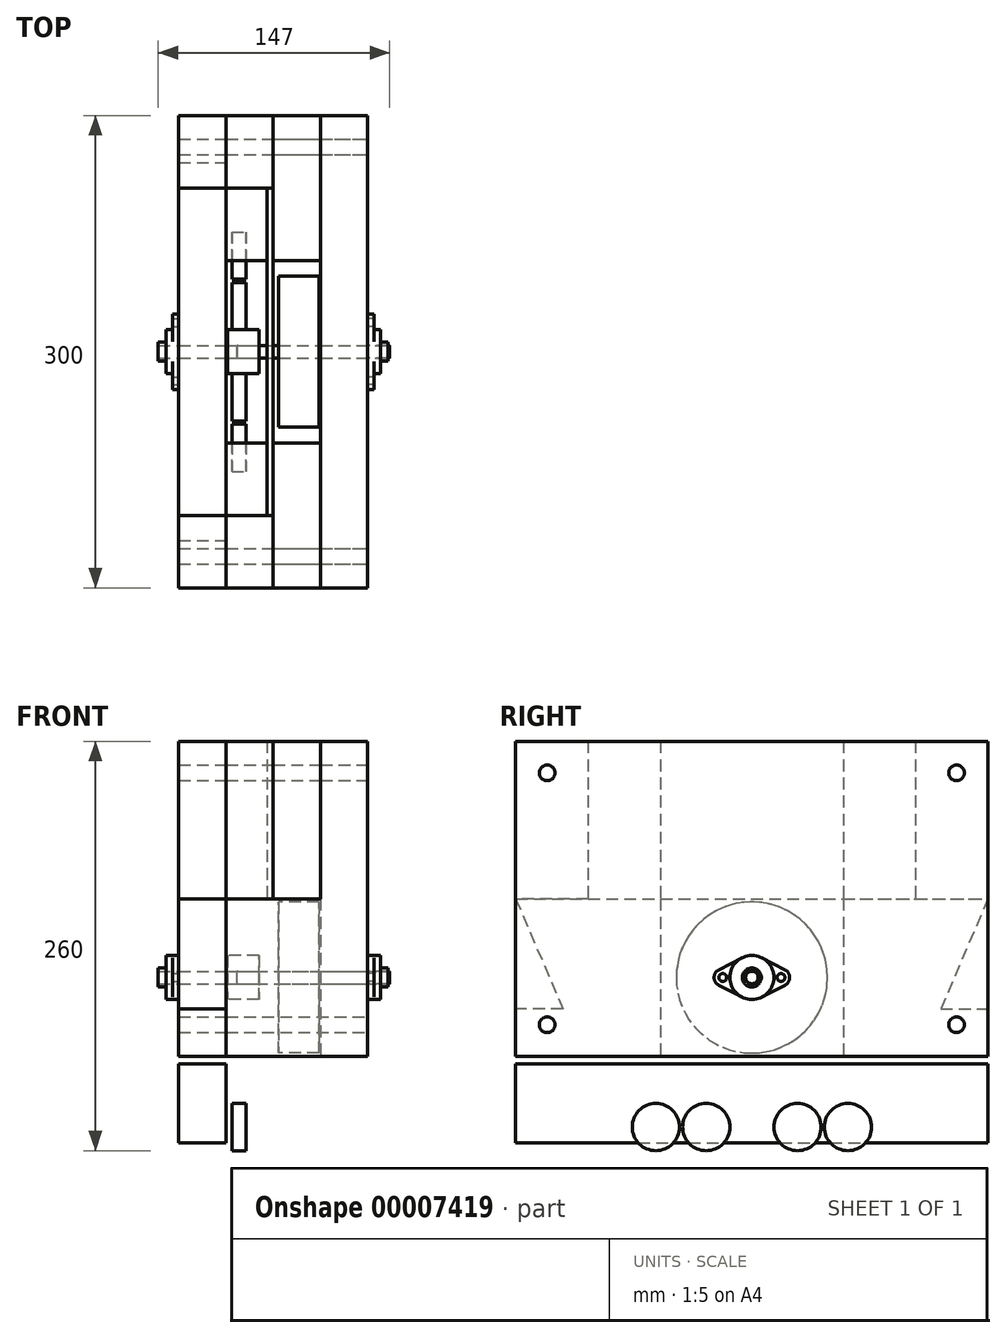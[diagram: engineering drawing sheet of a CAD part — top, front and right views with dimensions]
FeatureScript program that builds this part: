
annotation { "Feature Type Name" : "Feature", "Feature Type Description" : "" }
export const myFeature = defineFeature(function(context is Context, id is Id, definition is map)
    precondition{}
    {
        {
            var Q0;
            Q0=qCreatedBy(makeId("Front.planeOp"),FACE);
            var sketch = newSketch(context, id + "F0", { "sketchPlane" : qUnion([Q0])});
            skLineSegment(sketch, "E0.bottom", {"start": v(10, 14) * mm, "end": v(-10, 14) * mm});
            skLineSegment(sketch, "E0.top", {"start": v(10, -14) * mm, "end": v(4.5, -14) * mm});
            skLineSegment(sketch, "E0.left", {"start": v(10, 14) * mm, "end": v(10, -14) * mm});
            skLineSegment(sketch, "E0.right", {"start": v(-10, 14) * mm, "end": v(-10, -14) * mm});
            skPoint(sketch, "E0.middle", {"position": v(0, 0) * mm});
            skLineSegment(sketch, "E1", {"start": v(0, 0) * mm, "end": v(134.05, 0) * mm, "construction": true});
            skLineSegment(sketch, "E2", {"start": v(0, 0) * mm, "end": v(-79.2, 0) * mm, "construction": true});
            skLineSegment(sketch, "E3.bottom", {"start": v(-41, 15) * mm, "end": v(-56, 15) * mm});
            skLineSegment(sketch, "E3.top", {"start": v(-41, -15) * mm, "end": v(-56, -15) * mm});
            skLineSegment(sketch, "E3.left", {"start": v(-41, 15) * mm, "end": v(-41, -15) * mm});
            skLineSegment(sketch, "E3.right", {"start": v(-56, 15) * mm, "end": v(-56, -15) * mm});
            skPoint(sketch, "E3.middle", {"position": v(-48.5, 0) * mm});
            skLineSegment(sketch, "E4.bottom", {"start": v(48, 48) * mm, "end": v(32.5, 48) * mm});
            skLineSegment(sketch, "E4.top", {"start": v(48, -48) * mm, "end": v(22.5, -48) * mm});
            skLineSegment(sketch, "E4.left", {"start": v(48, 48) * mm, "end": v(48, -48) * mm});
            skLineSegment(sketch, "E4.right", {"start": v(22.5, 48) * mm, "end": v(22.5, -48) * mm});
            skPoint(sketch, "E4.middle", {"position": v(35.25, 0) * mm});
            skLineSegment(sketch, "E5.bottom", {"start": v(94, 15) * mm, "end": v(79, 15) * mm});
            skLineSegment(sketch, "E5.top", {"start": v(94, -15) * mm, "end": v(79, -15) * mm});
            skLineSegment(sketch, "E5.left", {"start": v(94, 15) * mm, "end": v(94, -15) * mm});
            skLineSegment(sketch, "E5.right", {"start": v(79, 15) * mm, "end": v(79, -15) * mm});
            skPoint(sketch, "E5.middle", {"position": v(86.5, 0) * mm});
            skLineSegment(sketch, "E6.bottom", {"start": v(24, 127.89) * mm, "end": v(54, 127.89) * mm});
            skLineSegment(sketch, "E6.top", {"start": v(24, 77.89) * mm, "end": v(54, 77.89) * mm});
            skLineSegment(sketch, "E6.left", {"start": v(24, 127.89) * mm, "end": v(24, 77.89) * mm});
            skLineSegment(sketch, "E6.right", {"start": v(54, 127.89) * mm, "end": v(54, 77.89) * mm});
            skLineSegment(sketch, "E7", {"start": v(54, 77.89) * mm, "end": v(64, 77.89) * mm});
            skLineSegment(sketch, "E8", {"start": v(64, 77.89) * mm, "end": v(64, 127.89) * mm});
            skLineSegment(sketch, "E9", {"start": v(64, 127.89) * mm, "end": v(54, 127.89) * mm});
            skLineSegment(sketch, "E10.bottom", {"start": v(79, 50) * mm, "end": v(49, 50) * mm});
            skLineSegment(sketch, "E10.top", {"start": v(79, -50) * mm, "end": v(49, -50) * mm});
            skLineSegment(sketch, "E10.left", {"start": v(79, 50) * mm, "end": v(79, -50) * mm});
            skLineSegment(sketch, "E10.right", {"start": v(49, 50) * mm, "end": v(49, -50) * mm});
            skPoint(sketch, "E10.middle", {"position": v(64, 0) * mm});
            skLineSegment(sketch, "E11.bottom", {"start": v(-11, 50) * mm, "end": v(-41, 50) * mm});
            skLineSegment(sketch, "E11.top", {"start": v(-11, -50) * mm, "end": v(-41, -50) * mm});
            skLineSegment(sketch, "E11.left", {"start": v(-11, 50) * mm, "end": v(-11, -50) * mm});
            skLineSegment(sketch, "E11.right", {"start": v(-41, 50) * mm, "end": v(-41, -50) * mm});
            skPoint(sketch, "E11.middle", {"position": v(-26, 0) * mm});
            skLineSegment(sketch, "E12.bottom", {"start": v(109, 150) * mm, "end": v(79, 150) * mm});
            skLineSegment(sketch, "E12.top", {"start": v(109, -150) * mm, "end": v(79, -150) * mm});
            skLineSegment(sketch, "E12.left", {"start": v(109, 150) * mm, "end": v(109, -150) * mm});
            skLineSegment(sketch, "E12.right", {"start": v(79, 150) * mm, "end": v(79, -150) * mm});
            skPoint(sketch, "E12.middle", {"position": v(94, 0) * mm});
            skLineSegment(sketch, "E13", {"start": v(64, 127.89) * mm, "end": v(79, 127.89) * mm, "construction": true});
            skLineSegment(sketch, "E14", {"start": v(64, 77.89) * mm, "end": v(79, 77.89) * mm, "construction": true});
            skLineSegment(sketch, "E15", {"start": v(32.5, 48) * mm, "end": v(32.5, -48) * mm, "construction": true});
            skLineSegment(sketch, "E16", {"start": v(32.5, 48) * mm, "end": v(22.5, 48) * mm});
            skLineSegment(sketch, "E17", {"start": v(59, 77.89) * mm, "end": v(59, 48) * mm, "construction": true});
            skPoint(sketch, "E18", {"position": v(40.25, 48) * mm});
            skLineSegment(sketch, "E19", {"start": v(48, 48) * mm, "end": v(48, 127.89) * mm, "construction": true});
            skLineSegment(sketch, "E20", {"start": v(54, 77.89) * mm, "end": v(54, 48) * mm, "construction": true});
            skLineSegment(sketch, "E21", {"start": v(64, 77.89) * mm, "end": v(64, 48) * mm, "construction": true});
            skCircle(sketch, "E22", {"center": v(46, 102.89) * mm, "radius": 8 * mm, "construction": true});
            skLineSegment(sketch, "E23", {"start": v(46, 102.89) * mm, "end": v(64, 102.89) * mm, "construction": true});
            skLineSegment(sketch, "E24.bottom", {"start": v(109, 127.89) * mm, "end": v(149, 127.89) * mm});
            skLineSegment(sketch, "E24.top", {"start": v(109, 77.89) * mm, "end": v(149, 77.89) * mm});
            skLineSegment(sketch, "E24.left", {"start": v(109, 127.89) * mm, "end": v(109, 77.89) * mm});
            skLineSegment(sketch, "E24.right", {"start": v(149, 127.89) * mm, "end": v(149, 77.89) * mm});
            skCircle(sketch, "E25", {"center": v(127, 102.89) * mm, "radius": 8 * mm, "construction": true});
            skLineSegment(sketch, "E26", {"start": v(127, 102.89) * mm, "end": v(109, 102.89) * mm, "construction": true});
            skLineSegment(sketch, "E27.bottom", {"start": v(-41, -55) * mm, "end": v(-11, -55) * mm});
            skLineSegment(sketch, "E27.top", {"start": v(-41, -105) * mm, "end": v(-11, -105) * mm});
            skLineSegment(sketch, "E27.left", {"start": v(-41, -55) * mm, "end": v(-41, -105) * mm});
            skLineSegment(sketch, "E27.right", {"start": v(-11, -55) * mm, "end": v(-11, -105) * mm});
            skLineSegment(sketch, "E28.bottom", {"start": v(22.5, -55) * mm, "end": v(79, -55) * mm});
            skLineSegment(sketch, "E28.top", {"start": v(22.5, -105) * mm, "end": v(79, -105) * mm});
            skLineSegment(sketch, "E28.left", {"start": v(22.5, -55) * mm, "end": v(22.5, -105) * mm});
            skLineSegment(sketch, "E28.right", {"start": v(79, -55) * mm, "end": v(79, -105) * mm});
            skLineSegment(sketch, "E29.bottom", {"start": v(1.75, -80) * mm, "end": v(-7.25, -80) * mm});
            skLineSegment(sketch, "E29.top", {"start": v(1.75, -110) * mm, "end": v(-7.25, -110) * mm});
            skLineSegment(sketch, "E29.left", {"start": v(1.75, -80) * mm, "end": v(1.75, -110) * mm});
            skLineSegment(sketch, "E29.right", {"start": v(-7.25, -80) * mm, "end": v(-7.25, -110) * mm});
            skPoint(sketch, "E29.middle", {"position": v(-2.75, -95) * mm});
            skLineSegment(sketch, "E30", {"start": v(4.5, 14) * mm, "end": v(4.5, -14) * mm, "construction": true});
            skLineSegment(sketch, "E31", {"start": v(4.5, -14) * mm, "end": v(-10, -14) * mm});
            skLineSegment(sketch, "E32", {"start": v(-2.75, -14) * mm, "end": v(-2.75, -95) * mm, "construction": true});
            skSolve(sketch);
        }
        {
            var Q0;
            Q0=qCreatedBy(makeId("Right.planeOp"),FACE);
            var sketch = newSketch(context, id + "F1", { "sketchPlane" : qUnion([Q0])});
            skPoint(sketch, "E33.0", {"position": v(0, 0) * mm});
            skCircle(sketch, "E34", {"center": v(0, 0) * mm, "radius": 14 * mm});
            skSolve(sketch);
        }
        {
            var Q0;
            Q0=qSketchRegion(id+"F1",true);
            extrude(context, id + "F2", {"entities" : qUnion([Q0]), "endBound" : BoundingType.SYMMETRIC, "depth" : 20 * mm});
        }
        {
            var Q0;
            Q0=sQuery(id+"F0.wireOp",EDGE,"E4.right");
            var Q1;
            Q1=makeQuery(id+"F2.opExtrude","CAP_FACE",FACE,{"disambiguationData":[OSD([sQuery(id+"F1.wireOp",EDGE,"E34")])],"isStart":false});
            cPlane(context, id + "F3", {"entities" : qUnion([Q0, Q1]), "cplaneType" : CPlaneType.LINE_ANGLE, "offset" : 25 * mm, "angle" : 0 * degree, "width" : 150 * mm, "height" : 150 * mm});
        }
        {
            var Q0;
            Q0=qCreatedBy(id+"F3.planeOp",FACE);
            var sketch = newSketch(context, id + "F4", { "sketchPlane" : qUnion([Q0])});
            skPoint(sketch, "E35.0", {"position": v(0, 0) * mm});
            skCircle(sketch, "E36", {"center": v(0, 0) * mm, "radius": 48 * mm});
            skSolve(sketch);
        }
        {
            var Q0;
            Q0=qSketchRegion(id+"F4",true);
            var Q1;
            Q1=sQuery(id+"F0.wireOp",VERTEX,"E4.left.start");
            extrude(context, id + "F5", {"entities" : qUnion([Q0]), "endBound" : BoundingType.UP_TO_VERTEX, "oppositeDirection" : true, "endBoundEntityVertex" : qUnion([Q1]), "depth" : 25 * mm});
        }
        {
            var Q0;
            {var subQ3=sQuery(id+"F0.wireOp",EDGE,"E10.bottom");Q0=makeQuery(id+"F0.imprint","IMPRINT",FACE,{"disambiguationData":[TD([[makeQuery(id+"F0.imprint","IMPRINT",EDGE,{"derivedFrom":subQ3}),1.0]])]});}
            extrude(context, id + "F6", {"entities" : qUnion([Q0]), "endBound" : BoundingType.SYMMETRIC, "depth" : 300 * mm});
        }
        {
            var Q0;
            {var subQ2=sQuery(id+"F0.wireOp",EDGE,"E11.bottom");Q0=makeQuery(id+"F0.imprint","IMPRINT",FACE,{"disambiguationData":[TD([[makeQuery(id+"F0.imprint","IMPRINT",EDGE,{"derivedFrom":subQ2}),1.0]])]});}
            extrude(context, id + "F7", {"entities" : qUnion([Q0]), "endBound" : BoundingType.SYMMETRIC, "depth" : 300 * mm});
        }
        {
            var Q0;
            Q0=makeQuery(id+"F6.opExtrude","SWEPT_FACE",FACE,{"disambiguationData":[OSD([sQuery(id+"F0.wireOp",EDGE,"E10.right")])]});
            var sketch = newSketch(context, id + "F8", { "sketchPlane" : qUnion([Q0])});
            skCircle(sketch, "E37.0", {"center": v(0, 0) * mm, "radius": 48 * mm, "construction": true});
            skLineSegment(sketch, "E38", {"start": v(48, 50) * mm, "end": v(48, -50) * mm, "construction": true});
            skLineSegment(sketch, "E39.bottom", {"start": v(150, 50) * mm, "end": v(58, 50) * mm});
            skLineSegment(sketch, "E39.top", {"start": v(150, -50) * mm, "end": v(58, -50) * mm});
            skLineSegment(sketch, "E39.left", {"start": v(150, 50) * mm, "end": v(150, -50) * mm});
            skLineSegment(sketch, "E39.right", {"start": v(58, 50) * mm, "end": v(58, -50) * mm});
            skLineSegment(sketch, "E40.bottom", {"start": v(-150, 50) * mm, "end": v(-58, 50) * mm});
            skLineSegment(sketch, "E40.top", {"start": v(-150, -50) * mm, "end": v(-58, -50) * mm});
            skLineSegment(sketch, "E40.left", {"start": v(-150, 50) * mm, "end": v(-150, -50) * mm});
            skLineSegment(sketch, "E40.right", {"start": v(-58, 50) * mm, "end": v(-58, -50) * mm});
            skSolve(sketch);
        }
        {
            var Q0;
            Q0=makeQuery(id+"F8.imprint","IMPRINT",FACE,{"disambiguationData":[TD([[makeQuery(id+"F8.imprint","IMPRINT",EDGE,{"derivedFrom":sQuery(id+"F8.wireOp",EDGE,"E39.bottom")}),1.0]])]});
            var Q1;
            Q1=makeQuery(id+"F7.opExtrude","SWEPT_FACE",FACE,{"disambiguationData":[OSD([sQuery(id+"F0.wireOp",EDGE,"E11.left")])]});
            extrude(context, id + "F9", {"entities" : qUnion([Q0]), "endBound" : BoundingType.UP_TO_SURFACE, "endBoundEntityFace" : qUnion([Q1]), "depth" : 25 * mm});
        }
        {
            var Q0;
            Q0=makeQuery(id+"F6.opExtrude","SWEPT_FACE",FACE,{"disambiguationData":[OSD([sQuery(id+"F0.wireOp",EDGE,"E12.right")])]});
            var Q1;
            Q1=makeQuery(id+"F7.opExtrude","SWEPT_FACE",FACE,{"disambiguationData":[OSD([sQuery(id+"F0.wireOp",EDGE,"E11.right")])]});
            cPlane(context, id + "F10", {"entities" : qUnion([Q0, Q1]), "cplaneType" : CPlaneType.MID_PLANE, "offset" : 25 * mm, "width" : 150 * mm, "height" : 150 * mm});
        }
        {
            var Q0;
            Q0=makeQuery(id+"F6.opExtrude","SWEPT_FACE",FACE,{"disambiguationData":[OSD([sQuery(id+"F0.wireOp",EDGE,"E12.right")])]});
            var sketch = newSketch(context, id + "F11", { "sketchPlane" : qUnion([Q0])});
            skCircle(sketch, "E41", {"center": v(0, 0) * mm, "radius": 4 * mm});
            skLineSegment(sketch, "E42", {"start": v(0, 0) * mm, "end": v(-18.5, 0) * mm, "construction": true});
            skCircle(sketch, "E43", {"center": v(-18.5, 0) * mm, "radius": 2.5 * mm});
            skLineSegment(sketch, "E44", {"start": v(0, 0) * mm, "end": v(0, 14) * mm, "construction": true});
            skLineSegment(sketch, "E45", {"start": v(-6.43, 12.43) * mm, "end": v(-21.03, 4.89) * mm});
            skLineSegment(sketch, "E46", {"start": v(-6.43, -12.43) * mm, "end": v(-21.03, -4.89) * mm});
            skLineSegment(sketch, "E47", {"start": v(-18.5, 0) * mm, "end": v(-30.47, 0) * mm, "construction": true});
            skPoint(sketch, "E48.visualSharp", {"position": v(-30.47, 0) * mm});
            skArc(sketch, "E48.filletArc", {"start": v(-21.03, 4.89) * mm, "mid": v(-24, 0) * mm, "end": v(-21.03, -4.89) * mm});
            skPoint(sketch, "E49", {"position": v(-24, 0) * mm});
            skPoint(sketch, "E49.positionSnap0", {"position": v(-24, 0) * mm});
            skLineSegment(sketch, "E50.MirrorCS", {"start": v(6.43, 12.43) * mm, "end": v(21.03, 4.89) * mm});
            skArc(sketch, "E51.MirrorCS", {"start": v(21.03, 4.89) * mm, "mid": v(24, 0) * mm, "end": v(21.03, -4.89) * mm});
            skLineSegment(sketch, "E52.MirrorCS", {"start": v(6.43, -12.43) * mm, "end": v(21.03, -4.89) * mm});
            skCircle(sketch, "E53.MirrorC", {"center": v(18.5, 0) * mm, "radius": 2.5 * mm});
            skArc(sketch, "E54", {"start": v(-6.43, 12.43) * mm, "mid": v(-14, 0) * mm, "end": v(-6.43, -12.43) * mm, "construction": true});
            skArc(sketch, "E55", {"start": v(-6.43, -12.43) * mm, "mid": v(0, -14) * mm, "end": v(6.43, -12.43) * mm});
            skArc(sketch, "E56", {"start": v(6.43, 12.43) * mm, "mid": v(0, 14) * mm, "end": v(-6.43, 12.43) * mm});
            skArc(sketch, "E57", {"start": v(6.43, -12.43) * mm, "mid": v(14, 0) * mm, "end": v(6.43, 12.43) * mm, "construction": true});
            skSolve(sketch);
        }
        {
            var Q0;
            Q0=qSketchRegion(id+"F11",true);
            extrude(context, id + "F12", {"entities" : qUnion([Q0]), "depth" : 4 * mm});
        }
        {
            var Q0;
            Q0=makeQuery(id+"F12.opExtrude","CAP_FACE",FACE,{"disambiguationData":[OSD([sQuery(id+"F11.wireOp",EDGE,"E41"),sQuery(id+"F11.wireOp",EDGE,"E43"),sQuery(id+"F11.wireOp",EDGE,"E45"),sQuery(id+"F11.wireOp",EDGE,"E46"),sQuery(id+"F11.wireOp",EDGE,"E48.filletArc"),sQuery(id+"F11.wireOp",EDGE,"E50.MirrorCS"),sQuery(id+"F11.wireOp",EDGE,"E51.MirrorCS"),sQuery(id+"F11.wireOp",EDGE,"E52.MirrorCS"),sQuery(id+"F11.wireOp",EDGE,"E53.MirrorC"),sQuery(id+"F11.wireOp",EDGE,"E55"),sQuery(id+"F11.wireOp",EDGE,"E56")])],"isStart":false});
            var sketch = newSketch(context, id + "F13", { "sketchPlane" : qUnion([Q0])});
            skCircle(sketch, "E58", {"center": v(0, 0) * mm, "radius": 14 * mm});
            skCircle(sketch, "E59", {"center": v(0, 0) * mm, "radius": 4 * mm});
            skSolve(sketch);
        }
        {
            var Q0;
            Q0=qSketchRegion(id+"F13",true);
            extrude(context, id + "F14", {"entities" : qUnion([Q0]), "operationType" : NewBodyOperationType.ADD, "depth" : 4 * mm});
        }
        {
            var Q0;
            Q0=makeQuery(id+"F14.opExtrude","CAP_FACE",FACE,{"disambiguationData":[OSD([sQuery(id+"F13.wireOp",EDGE,"E58"),sQuery(id+"F13.wireOp",EDGE,"E59")])],"isStart":false});
            var sketch = newSketch(context, id + "F15", { "sketchPlane" : qUnion([Q0])});
            skCircle(sketch, "E60.0", {"center": v(0, 0) * mm, "radius": 4 * mm});
            skCircle(sketch, "E61", {"center": v(0, 0) * mm, "radius": 6 * mm});
            skSolve(sketch);
        }
        {
            var Q0;
            Q0=qSketchRegion(id+"F15",true);
            extrude(context, id + "F16", {"entities" : qUnion([Q0]), "operationType" : NewBodyOperationType.ADD, "depth" : 5 * mm});
        }
        {
            var Q0;
            Q0=makeQuery(id+"F12.opExtrude","SWEPT_BODY",BODY,{"disambiguationData":[OSD([sQuery(id+"F11.wireOp",EDGE,"E41"),sQuery(id+"F11.wireOp",EDGE,"E43"),sQuery(id+"F11.wireOp",EDGE,"E45"),sQuery(id+"F11.wireOp",EDGE,"E46"),sQuery(id+"F11.wireOp",EDGE,"E48.filletArc"),sQuery(id+"F11.wireOp",EDGE,"E50.MirrorCS"),sQuery(id+"F11.wireOp",EDGE,"E51.MirrorCS"),sQuery(id+"F11.wireOp",EDGE,"E52.MirrorCS"),sQuery(id+"F11.wireOp",EDGE,"E53.MirrorC"),sQuery(id+"F11.wireOp",EDGE,"E55"),sQuery(id+"F11.wireOp",EDGE,"E56")])]});
            var Q1;
            Q1=qCreatedBy(id+"F10.planeOp",FACE);
            mirror(context, id + "F17", {"entities" : qUnion([Q0]), "mirrorPlane" : qUnion([Q1])});
        }
        {
            var Q0;
            Q0=makeQuery(id+"F6.opExtrude","SWEPT_FACE",FACE,{"disambiguationData":[OSD([sQuery(id+"F0.wireOp",EDGE,"E12.right")])]});
            var sketch = newSketch(context, id + "F18", { "sketchPlane" : qUnion([Q0])});
            skCircle(sketch, "E62", {"center": v(0, 0) * mm, "radius": 4 * mm});
            skSolve(sketch);
        }
        {
            var Q0;
            Q0=qSketchRegion(id+"F18",true);
            extrude(context, id + "F19", {"entities" : qUnion([Q0]), "operationType" : NewBodyOperationType.REMOVE, "endBound" : BoundingType.THROUGH_ALL, "oppositeDirection" : true, "depth" : 25 * mm});
        }
        {
            var Q0;
            Q0=makeQuery(id+"F0.imprint","IMPRINT",FACE,{"disambiguationData":[TD([[makeQuery(id+"F0.imprint","IMPRINT",EDGE,{"derivedFrom":sQuery(id+"F0.wireOp",EDGE,"E28.bottom")}),-1.0]])]});
            extrude(context, id + "F20", {"entities" : qUnion([Q0]), "endBound" : BoundingType.SYMMETRIC, "depth" : 200 * mm});
        }
        {
            var Q0;
            Q0=makeQuery(id+"F0.imprint","IMPRINT",FACE,{"disambiguationData":[TD([[makeQuery(id+"F0.imprint","IMPRINT",EDGE,{"derivedFrom":sQuery(id+"F0.wireOp",EDGE,"E27.bottom")}),-1.0]])]});
            extrude(context, id + "F21", {"entities" : qUnion([Q0]), "endBound" : BoundingType.SYMMETRIC, "depth" : 300 * mm});
        }
        {
            var Q0;
            Q0=sQuery(id+"F0.wireOp",EDGE,"E29.left");
            var Q1;
            Q1=makeQuery(id+"F20.opExtrude","SWEPT_FACE",FACE,{"disambiguationData":[OSD([sQuery(id+"F0.wireOp",EDGE,"E28.left")])]});
            cPlane(context, id + "F22", {"entities" : qUnion([Q0, Q1]), "cplaneType" : CPlaneType.LINE_ANGLE, "offset" : 25 * mm, "angle" : 0 * degree, "width" : 150 * mm, "height" : 150 * mm});
        }
        {
            var Q0;
            Q0=qCreatedBy(id+"F22.planeOp",FACE);
            var sketch = newSketch(context, id + "F23", { "sketchPlane" : qUnion([Q0])});
            skCircle(sketch, "E63.0", {"center": v(0, 0) * mm, "radius": 14 * mm, "construction": true});
            skLineSegment(sketch, "E64", {"start": v(0, 0) * mm, "end": v(0, -105) * mm, "construction": true});
            skPoint(sketch, "E65.0", {"position": v(0, -95) * mm});
            skLineSegment(sketch, "E66", {"start": v(0, -95) * mm, "end": v(-29, -95) * mm, "construction": true});
            skLineSegment(sketch, "E67", {"start": v(-29, -95) * mm, "end": v(-61, -95) * mm, "construction": true});
            skCircle(sketch, "E68", {"center": v(-29, -95) * mm, "radius": 15 * mm});
            skLineSegment(sketch, "E69", {"start": v(-14, 0) * mm, "end": v(-14, -95) * mm, "construction": true});
            skLineSegment(sketch, "E70", {"start": v(-14, 0) * mm, "end": v(0, 0) * mm, "construction": true});
            skCircle(sketch, "E71", {"center": v(-61, -95) * mm, "radius": 15 * mm});
            skPoint(sketch, "E72", {"position": v(-44, -95) * mm});
            skPoint(sketch, "E73", {"position": v(-46, -95) * mm});
            skCircle(sketch, "E74.MirrorC", {"center": v(29, -95) * mm, "radius": 15 * mm});
            skCircle(sketch, "E75.MirrorC", {"center": v(61, -95) * mm, "radius": 15 * mm});
            skSolve(sketch);
        }
        {
            var Q0;
            Q0=qSketchRegion(id+"F23",true);
            extrude(context, id + "F24", {"entities" : qUnion([Q0]), "oppositeDirection" : true, "depth" : 9 * mm});
        }
        {
            var Q0;
            Q0=makeQuery(id+"F6.opExtrude","CAP_FACE",FACE,{"disambiguationData":[OSD([sQuery(id+"F0.wireOp",EDGE,"E10.bottom"),sQuery(id+"F0.wireOp",EDGE,"E10.top"),sQuery(id+"F0.wireOp",EDGE,"E10.right"),sQuery(id+"F0.wireOp",EDGE,"E12.right")])],"isStart":false});
            var Q1;
            Q1=makeQuery(id+"F6.opExtrude","CAP_FACE",FACE,{"disambiguationData":[OSD([sQuery(id+"F0.wireOp",EDGE,"E10.bottom"),sQuery(id+"F0.wireOp",EDGE,"E10.top"),sQuery(id+"F0.wireOp",EDGE,"E10.right"),sQuery(id+"F0.wireOp",EDGE,"E12.right")])],"isStart":true});
            cPlane(context, id + "F25", {"entities" : qUnion([Q0, Q1]), "cplaneType" : CPlaneType.MID_PLANE, "offset" : 25 * mm, "width" : 150 * mm, "height" : 150 * mm});
        }
        {
            var Q0;
            Q0=makeQuery(id+"F9.opExtrude","SWEPT_BODY",BODY,{"disambiguationData":[OSD([sQuery(id+"F8.wireOp",EDGE,"E39.bottom"),sQuery(id+"F8.wireOp",EDGE,"E39.top"),sQuery(id+"F8.wireOp",EDGE,"E39.left"),sQuery(id+"F8.wireOp",EDGE,"E39.right")])]});
            var Q1;
            Q1=qCreatedBy(id+"F25.planeOp",FACE);
            mirror(context, id + "F26", {"entities" : qUnion([Q0]), "mirrorPlane" : qUnion([Q1])});
        }
        {
            var Q0;
            Q0=makeQuery(id+"F16.opExtrude","CAP_FACE",FACE,{"disambiguationData":[OSD([sQuery(id+"F15.wireOp",EDGE,"E60.0"),sQuery(id+"F15.wireOp",EDGE,"E61")])],"isStart":false});
            var sketch = newSketch(context, id + "F27", { "sketchPlane" : qUnion([Q0])});
            skCircle(sketch, "E76.0", {"center": v(0, 0) * mm, "radius": 4 * mm});
            skSolve(sketch);
        }
        {
            var Q0;
            Q0=qSketchRegion(id+"F27",true);
            extrude(context, id + "F28", {"entities" : qUnion([Q0]), "oppositeDirection" : true, "depth" : 96 * mm, "hasSecondDirection" : true, "secondDirectionOppositeDirection" : false, "secondDirectionDepth" : 1 * mm});
        }
        {
            var Q0;
            Q0=makeQuery(id+"F28.opExtrude","CAP_EDGE",EDGE,{"disambiguationData":[OSD([sQuery(id+"F27.wireOp",EDGE,"E76.0")])],"isStart":true});
            var Q1;
            Q1=makeQuery(id+"F28.opExtrude","CAP_EDGE",EDGE,{"disambiguationData":[OSD([sQuery(id+"F27.wireOp",EDGE,"E76.0")])],"isStart":false});
            fillet(context, id + "F29", {"entities" : qUnion([Q0, Q1]), "radius" : 0.5 * mm, "tangentPropagation" : true, "conicFillet" : false});
        }
        {
            var Q0;
            Q0=makeQuery(id+"F6.opExtrude","SWEPT_FACE",FACE,{"disambiguationData":[OSD([sQuery(id+"F0.wireOp",EDGE,"E10.bottom")])]});
            extrude(context, id + "F30", {"entities" : qUnion([Q0]), "operationType" : NewBodyOperationType.ADD, "depth" : 100 * mm});
        }
        {
            var Q0;
            {var subQ0=sQuery(id+"F0.wireOp",EDGE,"E10.right");Q0=makeQuery(id+"F30.boolean.opBoolean","MERGE",FACE,{"derivedFrom":[makeQuery(id+"F6.opExtrude","SWEPT_FACE",FACE,{"disambiguationData":[OSD([subQ0])]}),makeQuery(id+"F30.opExtrude","SWEPT_FACE",FACE,{"disambiguationData":[OSD([sQuery(id+"F0.wireOp",EDGE,"E10.bottom"),subQ0])]})]});}
            var sketch = newSketch(context, id + "F31", { "sketchPlane" : qUnion([Q0])});
            skLineSegment(sketch, "E77.bottom", {"start": v(150, 150) * mm, "end": v(58, 150) * mm});
            skLineSegment(sketch, "E77.top", {"start": v(150, 50) * mm, "end": v(58, 50) * mm});
            skLineSegment(sketch, "E77.left", {"start": v(150, 150) * mm, "end": v(150, 50) * mm});
            skLineSegment(sketch, "E77.right", {"start": v(58, 150) * mm, "end": v(58, 50) * mm});
            skLineSegment(sketch, "E78.bottom", {"start": v(-150, 150) * mm, "end": v(-58, 150) * mm});
            skLineSegment(sketch, "E78.top", {"start": v(-150, 50) * mm, "end": v(-58, 50) * mm});
            skLineSegment(sketch, "E78.left", {"start": v(-150, 150) * mm, "end": v(-150, 50) * mm});
            skLineSegment(sketch, "E78.right", {"start": v(-58, 150) * mm, "end": v(-58, 50) * mm});
            skSolve(sketch);
        }
        {
            var Q0;
            Q0 = qSketchRegion(id + "F31", true);
            extrude(context, id + "F32", {"entities" : qUnion([Q0]), "depth" : 30 * mm});
        }
        {
            var Q0;
            Q0=makeQuery(id+"F32.opExtrude","CAP_FACE",FACE,{"disambiguationData":[OSD([sQuery(id+"F31.wireOp",EDGE,"E77.bottom"),sQuery(id+"F31.wireOp",EDGE,"E77.top"),sQuery(id+"F31.wireOp",EDGE,"E77.left"),sQuery(id+"F31.wireOp",EDGE,"E77.right")])],"isStart":false});
            var sketch = newSketch(context, id + "F33", { "sketchPlane" : qUnion([Q0])});
            skLineSegment(sketch, "E79.bottom", {"start": v(104, 150) * mm, "end": v(-104, 150) * mm});
            skLineSegment(sketch, "E79.top", {"start": v(104, 50) * mm, "end": v(-104, 50) * mm});
            skLineSegment(sketch, "E79.left", {"start": v(104, 150) * mm, "end": v(104, 50) * mm});
            skLineSegment(sketch, "E79.right", {"start": v(-104, 150) * mm, "end": v(-104, 50) * mm});
            skSolve(sketch);
        }
        {
            var Q0;
            Q0 = qSketchRegion(id + "F33", true);
            extrude(context, id + "F34", {"entities" : qUnion([Q0]), "depth" : 4 * mm});
        }
        {
            var Q0;
            Q0=makeQuery(id+"F32.opExtrude","CAP_FACE",FACE,{"disambiguationData":[OSD([sQuery(id+"F31.wireOp",EDGE,"E78.bottom"),sQuery(id+"F31.wireOp",EDGE,"E78.top"),sQuery(id+"F31.wireOp",EDGE,"E78.left"),sQuery(id+"F31.wireOp",EDGE,"E78.right")])],"isStart":false});
            var sketch = newSketch(context, id + "F35", { "sketchPlane" : qUnion([Q0])});
            skLineSegment(sketch, "E80.0", {"start": v(-104, 150) * mm, "end": v(-104, 50) * mm});
            skLineSegment(sketch, "E81", {"start": v(-104, 150) * mm, "end": v(-150, 150) * mm});
            skLineSegment(sketch, "E82", {"start": v(-150, 150) * mm, "end": v(-150, 50) * mm});
            skLineSegment(sketch, "E83", {"start": v(-150, 50) * mm, "end": v(-104, 50) * mm});
            skSolve(sketch);
        }
        {
            var Q0;
            Q0 = qSketchRegion(id + "F35", true);
            extrude(context, id + "F36", {"entities" : qUnion([Q0]), "depth" : 30 * mm});
        }
        {
            var Q0;
            Q0=makeQuery(id+"F36.opExtrude","CAP_FACE",FACE,{"disambiguationData":[OSD([sQuery(id+"F35.wireOp",EDGE,"E80.0"),sQuery(id+"F35.wireOp",EDGE,"E81"),sQuery(id+"F35.wireOp",EDGE,"E82"),sQuery(id+"F35.wireOp",EDGE,"E83")])],"isStart":false});
            extrude(context, id + "F37", {"entities" : qUnion([Q0]), "depth" : 30 * mm});
        }
        {
            var Q0;
            Q0=makeQuery(id+"F36.opExtrude","SWEPT_BODY",BODY,{"disambiguationData":[OSD([sQuery(id+"F35.wireOp",EDGE,"E80.0"),sQuery(id+"F35.wireOp",EDGE,"E81"),sQuery(id+"F35.wireOp",EDGE,"E82"),sQuery(id+"F35.wireOp",EDGE,"E83")])]});
            var Q1;
            Q1=makeQuery(id+"F37.opExtrude","SWEPT_BODY",BODY,{"disambiguationData":[OSD([sQuery(id+"F35.wireOp",EDGE,"E80.0"),sQuery(id+"F35.wireOp",EDGE,"E81"),sQuery(id+"F35.wireOp",EDGE,"E82"),sQuery(id+"F35.wireOp",EDGE,"E83")])]});
            var Q2;
            Q2=qCreatedBy(makeId("Front.planeOp"),FACE);
            mirror(context, id + "F38", {"entities" : qUnion([Q0, Q1]), "mirrorPlane" : qUnion([Q2])});
        }
        {
            var Q0;
            Q0=makeQuery(id+"F7.opExtrude","SWEPT_FACE",FACE,{"disambiguationData":[OSD([sQuery(id+"F0.wireOp",EDGE,"E11.left")])]});
            var sketch = newSketch(context, id + "F39", { "sketchPlane" : qUnion([Q0])});
            skLineSegment(sketch, "E84", {"start": v(150, 50) * mm, "end": v(120, -20) * mm});
            skLineSegment(sketch, "E85", {"start": v(120, -20) * mm, "end": v(150, -20) * mm});
            skLineSegment(sketch, "E86", {"start": v(150, 50) * mm, "end": v(150, -20) * mm});
            skLineSegment(sketch, "E87", {"start": v(0, 50) * mm, "end": v(0, -50) * mm, "construction": true});
            skLineSegment(sketch, "E88.MirrorCS", {"start": v(-120, -20) * mm, "end": v(-150, -20) * mm});
            skLineSegment(sketch, "E89.MirrorCS", {"start": v(-150, 50) * mm, "end": v(-120, -20) * mm});
            skLineSegment(sketch, "E90.MirrorCS", {"start": v(-150, 50) * mm, "end": v(-150, -20) * mm});
            skSolve(sketch);
        }
        {
            var Q0;
            Q0 = qSketchRegion(id + "F39", true);
            extrude(context, id + "F40", {"entities" : qUnion([Q0]), "operationType" : NewBodyOperationType.REMOVE, "endBound" : BoundingType.THROUGH_ALL, "oppositeDirection" : true, "depth" : 25 * mm});
        }
        {
            var Q0;
            Q0=makeQuery(id+"F6.opExtrude","SWEPT_FACE",FACE,{"disambiguationData":[OSD([sQuery(id+"F0.wireOp",EDGE,"E12.right")])]});
            var sketch = newSketch(context, id + "F41", { "sketchPlane" : qUnion([Q0])});
            skLineSegment(sketch, "E91", {"start": v(-130, 150) * mm, "end": v(-130, 130) * mm, "construction": true});
            skLineSegment(sketch, "E92", {"start": v(-130, 130) * mm, "end": v(-130, 50) * mm, "construction": true});
            skLineSegment(sketch, "E93", {"start": v(-130, 50) * mm, "end": v(-130, -30) * mm, "construction": true});
            skLineSegment(sketch, "E94", {"start": v(-130, -30) * mm, "end": v(-130, -50) * mm, "construction": true});
            skCircle(sketch, "E95", {"center": v(-130, 130) * mm, "radius": 5 * mm});
            skCircle(sketch, "E96", {"center": v(-130, -30) * mm, "radius": 5 * mm});
            skLineSegment(sketch, "E97", {"start": v(0, 150) * mm, "end": v(0, -50) * mm, "construction": true});
            skCircle(sketch, "E98.MirrorC", {"center": v(130, 130) * mm, "radius": 5 * mm});
            skCircle(sketch, "E99.MirrorC", {"center": v(130, -30) * mm, "radius": 5 * mm});
            skSolve(sketch);
        }
        {
            var Q0;
            Q0=qSketchRegion(id+"F41",true);
            extrude(context, id + "F42", {"entities" : qUnion([Q0]), "operationType" : NewBodyOperationType.REMOVE, "endBound" : BoundingType.THROUGH_ALL, "oppositeDirection" : true, "depth" : 25 * mm});
        }
        {
            var Q0;
            Q0=makeQuery(id+"F20.opExtrude","SWEPT_BODY",BODY,{"disambiguationData":[OSD([sQuery(id+"F0.wireOp",EDGE,"E28.bottom"),sQuery(id+"F0.wireOp",EDGE,"E28.top"),sQuery(id+"F0.wireOp",EDGE,"E28.left"),sQuery(id+"F0.wireOp",EDGE,"E28.right")])]});
            deleteBodies(context, id + "F43", {"entities" : qUnion([Q0])});
        }
    });
